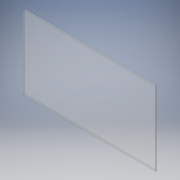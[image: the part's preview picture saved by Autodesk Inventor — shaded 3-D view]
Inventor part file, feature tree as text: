
AUTODESK INVENTOR PART (.ipt)
format: ipt  version: 2019 (Build 230136000, 136)  size: 94,208 bytes
history: native  units: in
note: dims shown in document units (in); Inventor stores cm internally (conversion verified against a paired STEP export)
features: extrude x1, sketch x1
ambient origin geometry x8: Origin, YZ Plane, XZ Plane, XY Plane, X Axis, Y Axis, Z Axis, Center Point
bodies: Solid1 (feature_tree)
feature tree (2):
  extrude  "Extrusion1"  Depth=3.356in
  sketch  "Sketch1"  dims[d0=6.0in d1=3.356in d2=0.073in d3=0.0in]
